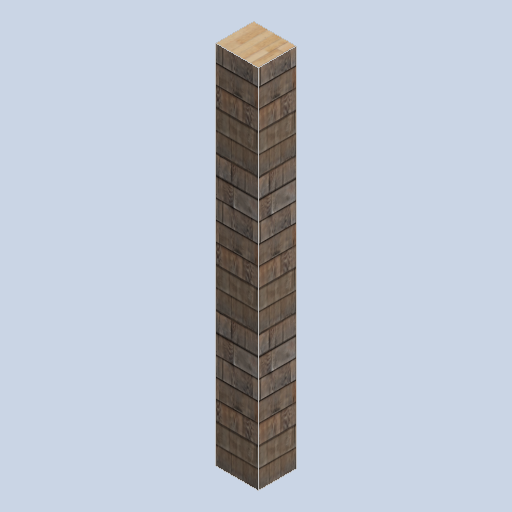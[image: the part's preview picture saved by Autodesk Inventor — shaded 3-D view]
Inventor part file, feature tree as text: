
AUTODESK INVENTOR PART (.ipt)
format: ipt  version: 2024.2 (Build 282272000, 272)  size: 167,424 bytes
history: native  units: in
note: dims shown in document units (in); Inventor stores cm internally (conversion verified against a paired STEP export)
features: other x3, sketch x1
ambient origin geometry x8: Origin, YZ Plane, XZ Plane, XY Plane, X Axis, Y Axis, Z Axis, Center Point
bodies: Solid1 (feature_tree)
feature tree (4):
  other  "support_column_01.ipt"
  other  "Solid1::support_column_01.ipt"
  other  "TaggingFeature1"
  sketch  "Sketch1"  dims[d0=0.3937in]
